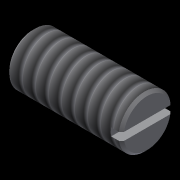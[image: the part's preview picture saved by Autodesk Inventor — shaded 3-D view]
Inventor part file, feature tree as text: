
AUTODESK INVENTOR PART (.ipt)
format: ipt  version: 2020 (Build 240168000, 168)  size: 100,352 bytes
history: native  units: mm
features: other x1, revolve x1, chamfer x1, thread x1, extrude x1
ambient origin geometry x8: Origin, YZ Plane, XZ Plane, XY Plane, X Axis, Y Axis, Z Axis, Center Point
bodies: Body1 (feature_tree)
feature tree (5):
  other  "實體1"
  revolve  "Revolution1"  Angle=90.0deg
  chamfer  "Chamfer1"  Distance=0.05mm Angle=45.0deg
  thread  "Thread4"  [1 undecoded]
  extrude  "Extrusion3"  Depth=2.2mm
note: 1 required parameter value undecoded (feature->parameter linkage not recoverable at this tier; creation-order binding heuristic only, values carry confidence <= 0.55)
